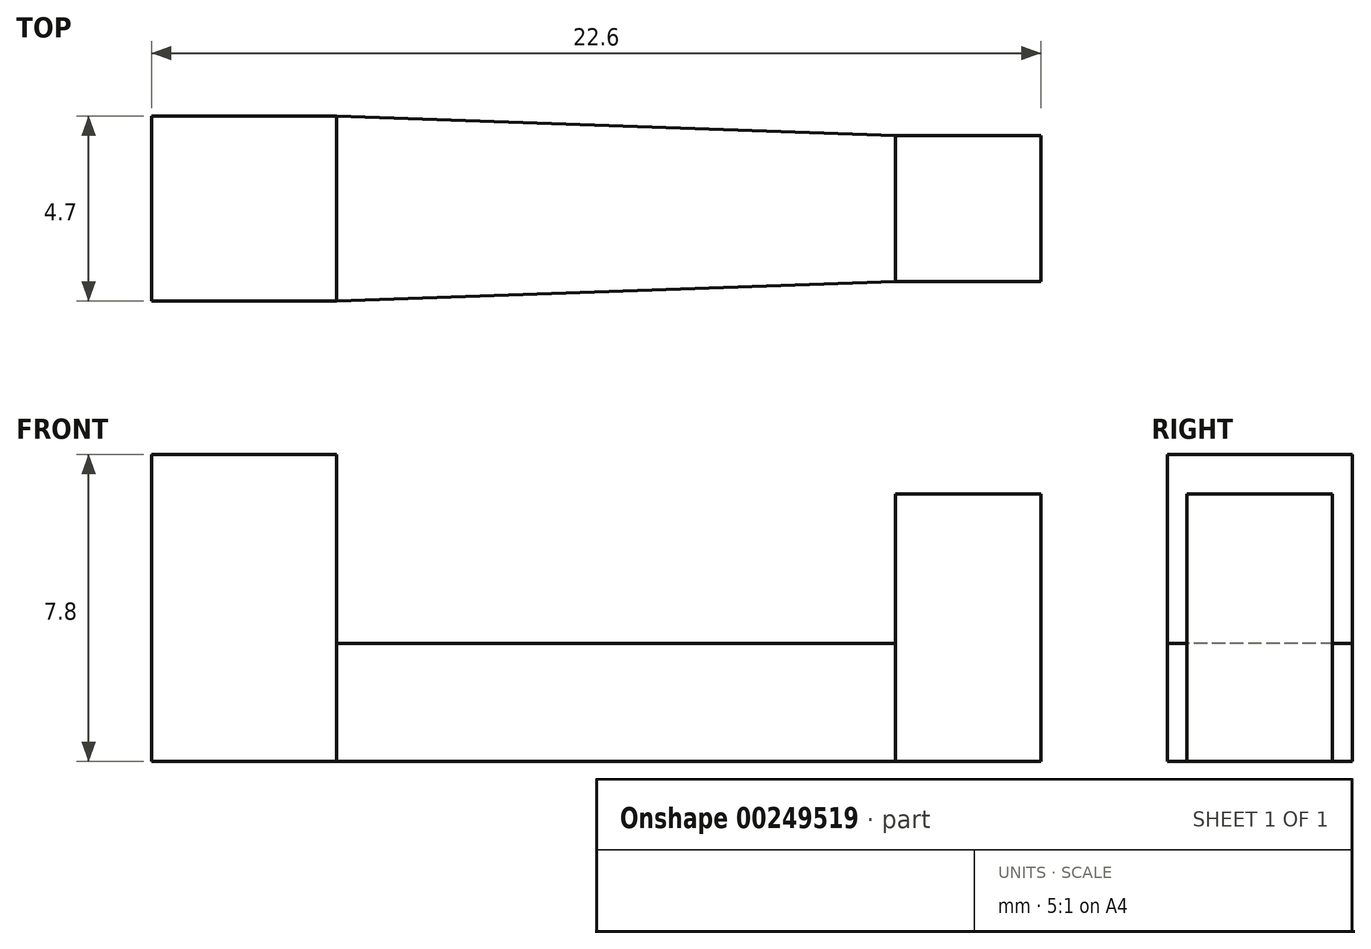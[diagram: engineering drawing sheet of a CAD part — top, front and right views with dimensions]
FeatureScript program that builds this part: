
annotation { "Feature Type Name" : "Feature", "Feature Type Description" : "" }
export const myFeature = defineFeature(function(context is Context, id is Id, definition is map)
    precondition{}
    {
        {
            var Q0;
            Q0=qCreatedBy(makeId("Top.planeOp"),FACE);
            var sketch = newSketch(context, id + "F0", { "sketchPlane" : qUnion([Q0])});
            skLineSegment(sketch, "E0", {"start": v(0, 1.85) * mm, "end": v(0, -1.85) * mm});
            skLineSegment(sketch, "E1", {"start": v(0, 1.85) * mm, "end": v(-14.2, 2.35) * mm});
            skLineSegment(sketch, "E2", {"start": v(-14.2, 2.35) * mm, "end": v(-14.2, -2.35) * mm});
            skLineSegment(sketch, "E3", {"start": v(-14.2, -2.35) * mm, "end": v(0, -1.85) * mm});
            skLineSegment(sketch, "E4", {"start": v(0, 0) * mm, "end": v(-14.2, 0) * mm});
            skPoint(sketch, "E4.endSnap0", {"position": v(-14.2, 0) * mm});
            skLineSegment(sketch, "E5", {"start": v(-14.2, 2.35) * mm, "end": v(-18.9, 2.35) * mm});
            skLineSegment(sketch, "E6", {"start": v(-18.9, 2.35) * mm, "end": v(-18.9, -2.35) * mm});
            skLineSegment(sketch, "E7", {"start": v(-18.9, -2.35) * mm, "end": v(-14.2, -2.35) * mm});
            skLineSegment(sketch, "E8", {"start": v(0, 1.85) * mm, "end": v(3.7, 1.85) * mm});
            skLineSegment(sketch, "E9", {"start": v(3.7, 1.85) * mm, "end": v(3.7, -1.85) * mm});
            skLineSegment(sketch, "E10", {"start": v(3.7, -1.85) * mm, "end": v(0, -1.85) * mm});
            skSolve(sketch);
        }
        {
            var Q0;
            {var subQ0=sQuery(id+"F0.wireOp",EDGE,"E5");Q0=makeQuery(id+"F0.imprint","IMPRINT",FACE,{"disambiguationData":[TD([[makeQuery(id+"F0.imprint","IMPRINT",EDGE,{"derivedFrom":subQ0}),1.0]])]});}
            extrude(context, id + "F1", {"entities" : qUnion([Q0]), "depth" : 7.8 * mm, "offsetDistance" : 25 * mm});
        }
        {
            var Q0;
            {var subQ0=sQuery(id+"F0.wireOp",EDGE,"E8");Q0=makeQuery(id+"F0.imprint","IMPRINT",FACE,{"disambiguationData":[TD([[makeQuery(id+"F0.imprint","IMPRINT",EDGE,{"derivedFrom":subQ0}),-1.0]])]});}
            extrude(context, id + "F2", {"entities" : qUnion([Q0]), "depth" : 6.8 * mm, "offsetDistance" : 25 * mm});
        }
        {
            var Q0;
            {var subQ0=sQuery(id+"F0.wireOp",EDGE,"E1");Q0=makeQuery(id+"F0.imprint","IMPRINT",FACE,{"disambiguationData":[TD([[makeQuery(id+"F0.imprint","IMPRINT",EDGE,{"derivedFrom":subQ0}),1.0]])]});}
            var Q1;
            {var subQ0=sQuery(id+"F0.wireOp",EDGE,"E3");Q1=makeQuery(id+"F0.imprint","IMPRINT",FACE,{"disambiguationData":[TD([[makeQuery(id+"F0.imprint","IMPRINT",EDGE,{"derivedFrom":subQ0}),1.0]])]});}
            extrude(context, id + "F3", {"entities" : qUnion([Q0, Q1]), "depth" : 3 * mm, "offsetDistance" : 25 * mm});
        }
    });
